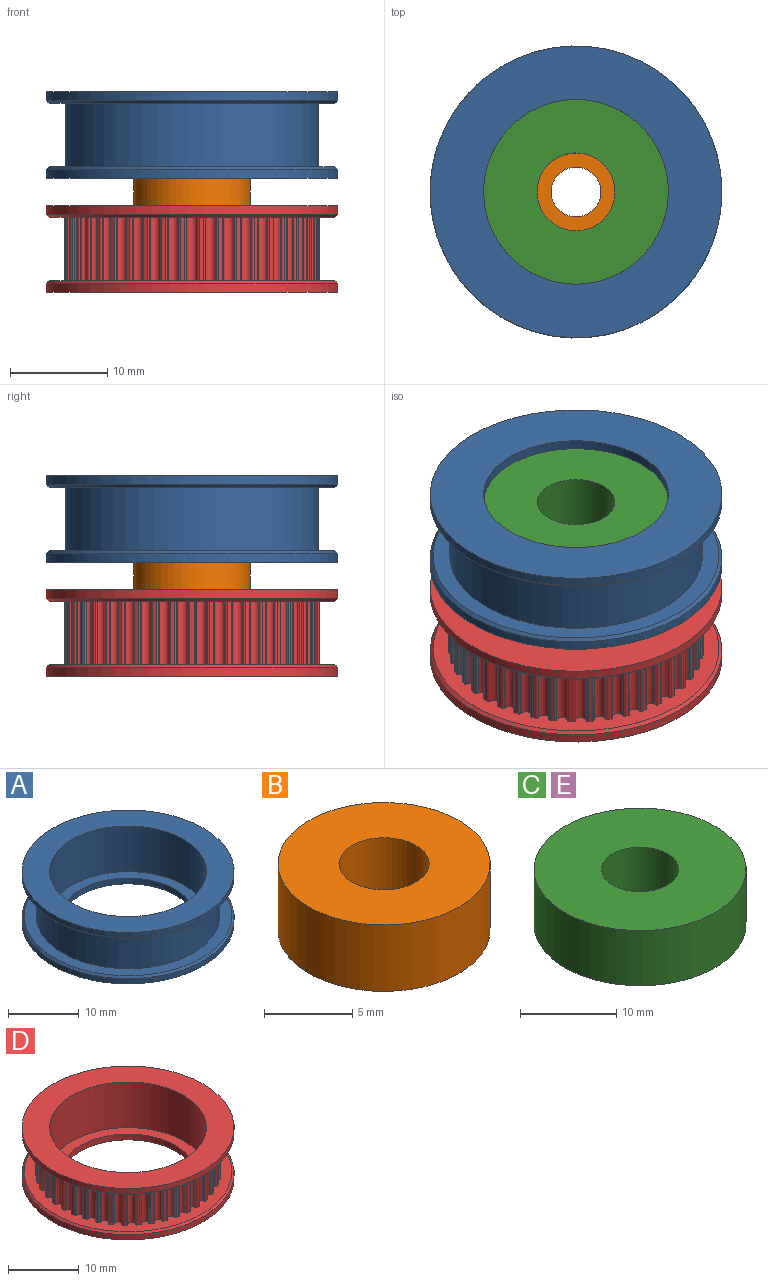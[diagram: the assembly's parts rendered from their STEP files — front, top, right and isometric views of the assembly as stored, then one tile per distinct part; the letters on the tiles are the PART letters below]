
ASSEMBLY  parts=5 mates=4
PART A: 12 faces, bbox 30x30x8.9 mm
  f0: plane 30x30mm, normal (0,0,1), area 319.8mm2, adj f6,f8
  f1: plane 30x30mm, normal (0,0,-1), area 423.3mm2, adj f2,f7
  f2: cylinder r=15mm len=30mm, axis (0,0,1), area 84.8mm2, adj f1,f11
  f3: plane 29.4x29.4mm, normal (0,0,1), area 147.9mm2, adj f4,f11
  f4: cylinder r=13mm len=26mm, axis (0,0,1), area 530.9mm2, adj f3,f5
  f5: plane 29.4x29.4mm, normal (0,0,-1), area 147.9mm2, adj f4,f10
  f6: cylinder r=15mm len=30mm, axis (0,0,1), area 84.8mm2, adj f0,f10
  f7: cylinder r=9.5mm len=19mm, axis (0,0,1), area 59.7mm2, adj f1,f9
  f8: cylinder r=11.1mm len=22.2mm, axis (0,0,1), area 551mm2, adj f0,f9
  f9: plane 22.2x22.2mm, normal (0,0,1), area 103.5mm2, adj f7,f8
  f10: cone r=15mm half-angle=45deg, axis (0,0,1), area 39.6mm2, adj f5,f6
  f11: cone r=14.7mm half-angle=45deg, axis (0,0,-1), area 39.6mm2, adj f2,f3
PART B: 4 faces, bbox 12x12x4.6 mm
  f0: cylinder r=2.55mm len=5.1mm, axis (0,0,-1), area 73.7mm2, adj f2,f3
  f1: cylinder r=6mm len=12mm, axis (0,0,-1), area 173.4mm2, adj f2,f3
  f2: plane 12x12mm, normal (0,0,1), area 92.7mm2, adj f0,f1
  f3: plane 12x12mm, normal (0,0,-1), area 92.7mm2, adj f0,f1
PART C: 4 faces, bbox 22x22x7 mm
  f0: cylinder r=4mm len=8mm, axis (0,0,-1), area 175.9mm2, adj f2,f3
  f1: cylinder r=11mm len=22mm, axis (0,0,-1), area 483.8mm2, adj f2,f3
  f2: plane 22x22mm, normal (0,0,1), area 329.9mm2, adj f0,f1
  f3: plane 22x22mm, normal (0,0,-1), area 329.9mm2, adj f0,f1
PART D: 263 faces, bbox 30x30x8.9 mm
  f0: cylinder r=13.12mm len=6.5mm, axis (0,0,-1), area 2.7mm2, adj f1,f12,f252,f255
  f1: cylinder r=0.19mm len=6.5mm, axis (0,0,-1), area 1.7mm2, adj f0,f2,f252,f255
  f2: cylinder r=5mm len=6.5mm, axis (0,0,-1), area 1.2mm2, adj f1,f3,f252,f255
  f3: cylinder r=0.56mm len=6.5mm, axis (0,0,-1), area 9.4mm2, adj f2,f4,f252,f255
  f4: cylinder r=5mm len=6.5mm, axis (0,0,-1), area 1.2mm2, adj f3,f5,f252,f255
  f5: cylinder r=0.19mm len=6.5mm, axis (0,0,-1), area 1.7mm2, adj f4,f6,f252,f255
  f6: cylinder r=13.12mm len=6.5mm, axis (0,0,-1), area 2.7mm2, adj f5,f247,f252,f255
  f7: cylinder r=13.12mm len=6.5mm, axis (0,0,-1), area 2.7mm2, adj f8,f18,f252,f255
  f8: cylinder r=0.19mm len=6.5mm, axis (0,0,-1), area 1.7mm2, adj f7,f9,f252,f255
  f9: cylinder r=5mm len=6.5mm, axis (0,0,-1), area 1.2mm2, adj f8,f10,f252,f255
  f10: cylinder r=0.56mm len=6.5mm, axis (0,0,-1), area 9.4mm2, adj f9,f11,f252,f255
  f11: cylinder r=5mm len=6.5mm, axis (0,0,-1), area 1.2mm2, adj f10,f12,f252,f255
  f12: cylinder r=0.19mm len=6.5mm, axis (0,0,-1), area 1.7mm2, adj f0,f11,f252,f255
  f13: cylinder r=13.12mm len=6.5mm, axis (0,0,-1), area 2.7mm2, adj f14,f24,f252,f255
  f14: cylinder r=0.19mm len=6.5mm, axis (0,0,-1), area 1.7mm2, adj f13,f15,f252,f255
  f15: cylinder r=5mm len=6.5mm, axis (0,0,-1), area 1.2mm2, adj f14,f16,f252,f255
  f16: cylinder r=0.56mm len=6.5mm, axis (0,0,-1), area 9.4mm2, adj f15,f17,f252,f255
  f17: cylinder r=5mm len=6.5mm, axis (0,0,-1), area 1.2mm2, adj f16,f18,f252,f255
  f18: cylinder r=0.19mm len=6.5mm, axis (0,0,-1), area 1.7mm2, adj f7,f17,f252,f255
  f19: cylinder r=13.12mm len=6.5mm, axis (0,0,-1), area 2.7mm2, adj f20,f30,f252,f255
  f20: cylinder r=0.19mm len=6.5mm, axis (0,0,-1), area 1.7mm2, adj f19,f21,f252,f255
  f21: cylinder r=5mm len=6.5mm, axis (0,0,-1), area 1.2mm2, adj f20,f22,f252,f255
  f22: cylinder r=0.56mm len=6.5mm, axis (0,0,-1), area 9.4mm2, adj f21,f23,f252,f255
  f23: cylinder r=5mm len=6.5mm, axis (0,0,-1), area 1.2mm2, adj f22,f24,f252,f255
  f24: cylinder r=0.19mm len=6.5mm, axis (0,0,-1), area 1.7mm2, adj f13,f23,f252,f255
  f25: cylinder r=13.12mm len=6.5mm, axis (0,0,-1), area 2.7mm2, adj f26,f36,f252,f255
  f26: cylinder r=0.19mm len=6.5mm, axis (0,0,-1), area 1.7mm2, adj f25,f27,f252,f255
  f27: cylinder r=5mm len=6.5mm, axis (0,0,-1), area 1.2mm2, adj f26,f28,f252,f255
  f28: cylinder r=0.56mm len=6.5mm, axis (0,0,-1), area 9.4mm2, adj f27,f29,f252,f255
  f29: cylinder r=5mm len=6.5mm, axis (0,0,-1), area 1.2mm2, adj f28,f30,f252,f255
  f30: cylinder r=0.19mm len=6.5mm, axis (0,0,-1), area 1.7mm2, adj f19,f29,f252,f255
  f31: cylinder r=13.12mm len=6.5mm, axis (0,0,-1), area 2.7mm2, adj f32,f42,f252,f255
  f32: cylinder r=0.19mm len=6.5mm, axis (0,0,-1), area 1.7mm2, adj f31,f33,f252,f255
  f33: cylinder r=5mm len=6.5mm, axis (0,0,-1), area 1.2mm2, adj f32,f34,f252,f255
  f34: cylinder r=0.56mm len=6.5mm, axis (0,0,-1), area 9.4mm2, adj f33,f35,f252,f255
  f35: cylinder r=5mm len=6.5mm, axis (0,0,-1), area 1.2mm2, adj f34,f36,f252,f255
  f36: cylinder r=0.19mm len=6.5mm, axis (0,0,-1), area 1.7mm2, adj f25,f35,f252,f255
  f37: cylinder r=13.12mm len=6.5mm, axis (0,0,-1), area 2.7mm2, adj f38,f48,f252,f255
  f38: cylinder r=0.19mm len=6.5mm, axis (0,0,-1), area 1.7mm2, adj f37,f39,f252,f255
  f39: cylinder r=5mm len=6.5mm, axis (0,0,-1), area 1.2mm2, adj f38,f40,f252,f255
  f40: cylinder r=0.56mm len=6.5mm, axis (0,0,-1), area 9.4mm2, adj f39,f41,f252,f255
  f41: cylinder r=5mm len=6.5mm, axis (0,0,-1), area 1.2mm2, adj f40,f42,f252,f255
  f42: cylinder r=0.19mm len=6.5mm, axis (0,0,-1), area 1.7mm2, adj f31,f41,f252,f255
  f43: cylinder r=13.12mm len=6.5mm, axis (0,0,-1), area 2.7mm2, adj f44,f54,f252,f255
  f44: cylinder r=0.19mm len=6.5mm, axis (0,0,-1), area 1.7mm2, adj f43,f45,f252,f255
  f45: cylinder r=5mm len=6.5mm, axis (0,0,-1), area 1.2mm2, adj f44,f46,f252,f255
  f46: cylinder r=0.56mm len=6.5mm, axis (0,0,-1), area 9.4mm2, adj f45,f47,f252,f255
  f47: cylinder r=5mm len=6.5mm, axis (0,0,-1), area 1.2mm2, adj f46,f48,f252,f255
  f48: cylinder r=0.19mm len=6.5mm, axis (0,0,-1), area 1.7mm2, adj f37,f47,f252,f255
  f49: cylinder r=13.12mm len=6.5mm, axis (0,0,-1), area 2.7mm2, adj f50,f60,f252,f255
  f50: cylinder r=0.19mm len=6.5mm, axis (0,0,-1), area 1.7mm2, adj f49,f51,f252,f255
  f51: cylinder r=5mm len=6.5mm, axis (0,0,-1), area 1.2mm2, adj f50,f52,f252,f255
  f52: cylinder r=0.56mm len=6.5mm, axis (0,0,-1), area 9.4mm2, adj f51,f53,f252,f255
  f53: cylinder r=5mm len=6.5mm, axis (0,0,-1), area 1.2mm2, adj f52,f54,f252,f255
  f54: cylinder r=0.19mm len=6.5mm, axis (0,0,-1), area 1.7mm2, adj f43,f53,f252,f255
  f55: cylinder r=13.12mm len=6.5mm, axis (0,0,-1), area 2.7mm2, adj f56,f66,f252,f255
  f56: cylinder r=0.19mm len=6.5mm, axis (0,0,-1), area 1.7mm2, adj f55,f57,f252,f255
  f57: cylinder r=5mm len=6.5mm, axis (0,0,-1), area 1.2mm2, adj f56,f58,f252,f255
  f58: cylinder r=0.56mm len=6.5mm, axis (0,0,-1), area 9.4mm2, adj f57,f59,f252,f255
  f59: cylinder r=5mm len=6.5mm, axis (0,0,-1), area 1.2mm2, adj f58,f60,f252,f255
  f60: cylinder r=0.19mm len=6.5mm, axis (0,0,-1), area 1.7mm2, adj f49,f59,f252,f255
  f61: cylinder r=13.12mm len=6.5mm, axis (0,0,-1), area 2.7mm2, adj f62,f72,f252,f255
  f62: cylinder r=0.19mm len=6.5mm, axis (0,0,-1), area 1.7mm2, adj f61,f63,f252,f255
  f63: cylinder r=5mm len=6.5mm, axis (0,0,-1), area 1.2mm2, adj f62,f64,f252,f255
  f64: cylinder r=0.56mm len=6.5mm, axis (0,0,-1), area 9.4mm2, adj f63,f65,f252,f255
  f65: cylinder r=5mm len=6.5mm, axis (0,0,-1), area 1.2mm2, adj f64,f66,f252,f255
  f66: cylinder r=0.19mm len=6.5mm, axis (0,0,-1), area 1.7mm2, adj f55,f65,f252,f255
  f67: cylinder r=13.12mm len=6.5mm, axis (0,0,-1), area 2.7mm2, adj f68,f78,f252,f255
  f68: cylinder r=0.19mm len=6.5mm, axis (0,0,-1), area 1.7mm2, adj f67,f69,f252,f255
  f69: cylinder r=5mm len=6.5mm, axis (0,0,-1), area 1.2mm2, adj f68,f70,f252,f255
  f70: cylinder r=0.56mm len=6.5mm, axis (0,0,-1), area 9.4mm2, adj f69,f71,f252,f255
  f71: cylinder r=5mm len=6.5mm, axis (0,0,-1), area 1.2mm2, adj f70,f72,f252,f255
  f72: cylinder r=0.19mm len=6.5mm, axis (0,0,-1), area 1.7mm2, adj f61,f71,f252,f255
  f73: cylinder r=13.12mm len=6.5mm, axis (0,0,-1), area 2.7mm2, adj f74,f84,f252,f255
  f74: cylinder r=0.19mm len=6.5mm, axis (0,0,-1), area 1.7mm2, adj f73,f75,f252,f255
  f75: cylinder r=5mm len=6.5mm, axis (0,0,-1), area 1.2mm2, adj f74,f76,f252,f255
  f76: cylinder r=0.56mm len=6.5mm, axis (0,0,-1), area 9.4mm2, adj f75,f77,f252,f255
  f77: cylinder r=5mm len=6.5mm, axis (0,0,-1), area 1.2mm2, adj f76,f78,f252,f255
  f78: cylinder r=0.19mm len=6.5mm, axis (0,0,-1), area 1.7mm2, adj f67,f77,f252,f255
  f79: cylinder r=13.12mm len=6.5mm, axis (0,0,-1), area 2.7mm2, adj f80,f90,f252,f255
  f80: cylinder r=0.19mm len=6.5mm, axis (0,0,-1), area 1.7mm2, adj f79,f81,f252,f255
  f81: cylinder r=5mm len=6.5mm, axis (0,0,-1), area 1.2mm2, adj f80,f82,f252,f255
  f82: cylinder r=0.56mm len=6.5mm, axis (0,0,-1), area 9.4mm2, adj f81,f83,f252,f255
  f83: cylinder r=5mm len=6.5mm, axis (0,0,-1), area 1.2mm2, adj f82,f84,f252,f255
  f84: cylinder r=0.19mm len=6.5mm, axis (0,0,-1), area 1.7mm2, adj f73,f83,f252,f255
  f85: cylinder r=13.12mm len=6.5mm, axis (0,0,-1), area 2.7mm2, adj f86,f96,f252,f255
  f86: cylinder r=0.19mm len=6.5mm, axis (0,0,-1), area 1.7mm2, adj f85,f87,f252,f255
  f87: cylinder r=5mm len=6.5mm, axis (0,0,-1), area 1.2mm2, adj f86,f88,f252,f255
  f88: cylinder r=0.56mm len=6.5mm, axis (0,0,-1), area 9.4mm2, adj f87,f89,f252,f255
  f89: cylinder r=5mm len=6.5mm, axis (0,0,-1), area 1.2mm2, adj f88,f90,f252,f255
  f90: cylinder r=0.19mm len=6.5mm, axis (0,0,-1), area 1.7mm2, adj f79,f89,f252,f255
  f91: cylinder r=13.12mm len=6.5mm, axis (0,0,-1), area 2.7mm2, adj f92,f102,f252,f255
  f92: cylinder r=0.19mm len=6.5mm, axis (0,0,-1), area 1.7mm2, adj f91,f93,f252,f255
  f93: cylinder r=5mm len=6.5mm, axis (0,0,-1), area 1.2mm2, adj f92,f94,f252,f255
  f94: cylinder r=0.56mm len=6.5mm, axis (0,0,-1), area 9.4mm2, adj f93,f95,f252,f255
  f95: cylinder r=5mm len=6.5mm, axis (0,0,-1), area 1.2mm2, adj f94,f96,f252,f255
  f96: cylinder r=0.19mm len=6.5mm, axis (0,0,-1), area 1.7mm2, adj f85,f95,f252,f255
  f97: cylinder r=13.12mm len=6.5mm, axis (0,0,-1), area 2.7mm2, adj f98,f108,f252,f255
  f98: cylinder r=0.19mm len=6.5mm, axis (0,0,-1), area 1.7mm2, adj f97,f99,f252,f255
  f99: cylinder r=5mm len=6.5mm, axis (0,0,-1), area 1.2mm2, adj f98,f100,f252,f255
  f100: cylinder r=0.56mm len=6.5mm, axis (0,0,-1), area 9.4mm2, adj f99,f101,f252,f255
  f101: cylinder r=5mm len=6.5mm, axis (0,0,-1), area 1.2mm2, adj f100,f102,f252,f255
  f102: cylinder r=0.19mm len=6.5mm, axis (0,0,-1), area 1.7mm2, adj f91,f101,f252,f255
  f103: cylinder r=13.12mm len=6.5mm, axis (0,0,-1), area 2.7mm2, adj f104,f114,f252,f255
  f104: cylinder r=0.19mm len=6.5mm, axis (0,0,-1), area 1.7mm2, adj f103,f105,f252,f255
  f105: cylinder r=5mm len=6.5mm, axis (0,0,-1), area 1.2mm2, adj f104,f106,f252,f255
  f106: cylinder r=0.56mm len=6.5mm, axis (0,0,-1), area 9.4mm2, adj f105,f107,f252,f255
  f107: cylinder r=5mm len=6.5mm, axis (0,0,-1), area 1.2mm2, adj f106,f108,f252,f255
  f108: cylinder r=0.19mm len=6.5mm, axis (0,0,-1), area 1.7mm2, adj f97,f107,f252,f255
  f109: cylinder r=13.12mm len=6.5mm, axis (0,0,-1), area 2.7mm2, adj f110,f120,f252,f255
  f110: cylinder r=0.19mm len=6.5mm, axis (0,0,-1), area 1.7mm2, adj f109,f111,f252,f255
  f111: cylinder r=5mm len=6.5mm, axis (0,0,-1), area 1.2mm2, adj f110,f112,f252,f255
  f112: cylinder r=0.56mm len=6.5mm, axis (0,0,-1), area 9.4mm2, adj f111,f113,f252,f255
  f113: cylinder r=5mm len=6.5mm, axis (0,0,-1), area 1.2mm2, adj f112,f114,f252,f255
  f114: cylinder r=0.19mm len=6.5mm, axis (0,0,-1), area 1.7mm2, adj f103,f113,f252,f255
  f115: cylinder r=13.12mm len=6.5mm, axis (0,0,-1), area 2.7mm2, adj f116,f126,f252,f255
  f116: cylinder r=0.19mm len=6.5mm, axis (0,0,-1), area 1.7mm2, adj f115,f117,f252,f255
  f117: cylinder r=5mm len=6.5mm, axis (0,0,-1), area 1.2mm2, adj f116,f118,f252,f255
  f118: cylinder r=0.56mm len=6.5mm, axis (0,0,-1), area 9.4mm2, adj f117,f119,f252,f255
  f119: cylinder r=5mm len=6.5mm, axis (0,0,-1), area 1.2mm2, adj f118,f120,f252,f255
  f120: cylinder r=0.19mm len=6.5mm, axis (0,0,-1), area 1.7mm2, adj f109,f119,f252,f255
  f121: cylinder r=13.12mm len=6.5mm, axis (0,0,-1), area 2.7mm2, adj f122,f132,f252,f255
  f122: cylinder r=0.19mm len=6.5mm, axis (0,0,-1), area 1.7mm2, adj f121,f123,f252,f255
  f123: cylinder r=5mm len=6.5mm, axis (0,0,-1), area 1.2mm2, adj f122,f124,f252,f255
  f124: cylinder r=0.56mm len=6.5mm, axis (0,0,-1), area 9.4mm2, adj f123,f125,f252,f255
  f125: cylinder r=5mm len=6.5mm, axis (0,0,-1), area 1.2mm2, adj f124,f126,f252,f255
  f126: cylinder r=0.19mm len=6.5mm, axis (0,0,-1), area 1.7mm2, adj f115,f125,f252,f255
  f127: cylinder r=13.12mm len=6.5mm, axis (0,0,-1), area 2.7mm2, adj f128,f138,f252,f255
  f128: cylinder r=0.19mm len=6.5mm, axis (0,0,-1), area 1.7mm2, adj f127,f129,f252,f255
  f129: cylinder r=5mm len=6.5mm, axis (0,0,-1), area 1.2mm2, adj f128,f130,f252,f255
  f130: cylinder r=0.56mm len=6.5mm, axis (0,0,-1), area 9.4mm2, adj f129,f131,f252,f255
  f131: cylinder r=5mm len=6.5mm, axis (0,0,-1), area 1.2mm2, adj f130,f132,f252,f255
  f132: cylinder r=0.19mm len=6.5mm, axis (0,0,-1), area 1.7mm2, adj f121,f131,f252,f255
  f133: cylinder r=13.12mm len=6.5mm, axis (0,0,-1), area 2.7mm2, adj f134,f144,f252,f255
  f134: cylinder r=0.19mm len=6.5mm, axis (0,0,-1), area 1.7mm2, adj f133,f135,f252,f255
  f135: cylinder r=5mm len=6.5mm, axis (0,0,-1), area 1.2mm2, adj f134,f136,f252,f255
  f136: cylinder r=0.56mm len=6.5mm, axis (0,0,-1), area 9.4mm2, adj f135,f137,f252,f255
  f137: cylinder r=5mm len=6.5mm, axis (0,0,-1), area 1.2mm2, adj f136,f138,f252,f255
  f138: cylinder r=0.19mm len=6.5mm, axis (0,0,-1), area 1.7mm2, adj f127,f137,f252,f255
  f139: cylinder r=13.12mm len=6.5mm, axis (0,0,-1), area 2.7mm2, adj f140,f150,f252,f255
  f140: cylinder r=0.19mm len=6.5mm, axis (0,0,-1), area 1.7mm2, adj f139,f141,f252,f255
  f141: cylinder r=5mm len=6.5mm, axis (0,0,-1), area 1.2mm2, adj f140,f142,f252,f255
  f142: cylinder r=0.56mm len=6.5mm, axis (0,0,-1), area 9.4mm2, adj f141,f143,f252,f255
  f143: cylinder r=5mm len=6.5mm, axis (0,0,-1), area 1.2mm2, adj f142,f144,f252,f255
  f144: cylinder r=0.19mm len=6.5mm, axis (0,0,-1), area 1.7mm2, adj f133,f143,f252,f255
  f145: cylinder r=13.12mm len=6.5mm, axis (0,0,-1), area 2.7mm2, adj f146,f156,f252,f255
  f146: cylinder r=0.19mm len=6.5mm, axis (0,0,-1), area 1.7mm2, adj f145,f147,f252,f255
  f147: cylinder r=5mm len=6.5mm, axis (0,0,-1), area 1.2mm2, adj f146,f148,f252,f255
  f148: cylinder r=0.56mm len=6.5mm, axis (0,0,-1), area 9.4mm2, adj f147,f149,f252,f255
  f149: cylinder r=5mm len=6.5mm, axis (0,0,-1), area 1.2mm2, adj f148,f150,f252,f255
  f150: cylinder r=0.19mm len=6.5mm, axis (0,0,-1), area 1.7mm2, adj f139,f149,f252,f255
  f151: cylinder r=13.12mm len=6.5mm, axis (0,0,-1), area 2.7mm2, adj f152,f162,f252,f255
  f152: cylinder r=0.19mm len=6.5mm, axis (0,0,-1), area 1.7mm2, adj f151,f153,f252,f255
  f153: cylinder r=5mm len=6.5mm, axis (0,0,-1), area 1.2mm2, adj f152,f154,f252,f255
  f154: cylinder r=0.56mm len=6.5mm, axis (0,0,-1), area 9.4mm2, adj f153,f155,f252,f255
  f155: cylinder r=5mm len=6.5mm, axis (0,0,-1), area 1.2mm2, adj f154,f156,f252,f255
  f156: cylinder r=0.19mm len=6.5mm, axis (0,0,-1), area 1.7mm2, adj f145,f155,f252,f255
  f157: cylinder r=13.12mm len=6.5mm, axis (0,0,-1), area 2.7mm2, adj f158,f168,f252,f255
  f158: cylinder r=0.19mm len=6.5mm, axis (0,0,-1), area 1.7mm2, adj f157,f159,f252,f255
  f159: cylinder r=5mm len=6.5mm, axis (0,0,-1), area 1.2mm2, adj f158,f160,f252,f255
  f160: cylinder r=0.56mm len=6.5mm, axis (0,0,-1), area 9.4mm2, adj f159,f161,f252,f255
  f161: cylinder r=5mm len=6.5mm, axis (0,0,-1), area 1.2mm2, adj f160,f162,f252,f255
  f162: cylinder r=0.19mm len=6.5mm, axis (0,0,-1), area 1.7mm2, adj f151,f161,f252,f255
  f163: cylinder r=13.12mm len=6.5mm, axis (0,0,-1), area 2.7mm2, adj f164,f174,f252,f255
  f164: cylinder r=0.19mm len=6.5mm, axis (0,0,-1), area 1.7mm2, adj f163,f165,f252,f255
  f165: cylinder r=5mm len=6.5mm, axis (0,0,-1), area 1.2mm2, adj f164,f166,f252,f255
  f166: cylinder r=0.56mm len=6.5mm, axis (0,0,-1), area 9.4mm2, adj f165,f167,f252,f255
  f167: cylinder r=5mm len=6.5mm, axis (0,0,-1), area 1.2mm2, adj f166,f168,f252,f255
  f168: cylinder r=0.19mm len=6.5mm, axis (0,0,-1), area 1.7mm2, adj f157,f167,f252,f255
  f169: cylinder r=13.12mm len=6.5mm, axis (0,0,-1), area 2.7mm2, adj f170,f180,f252,f255
  f170: cylinder r=0.19mm len=6.5mm, axis (0,0,-1), area 1.7mm2, adj f169,f171,f252,f255
  f171: cylinder r=5mm len=6.5mm, axis (0,0,-1), area 1.2mm2, adj f170,f172,f252,f255
  f172: cylinder r=0.56mm len=6.5mm, axis (0,0,-1), area 9.4mm2, adj f171,f173,f252,f255
  f173: cylinder r=5mm len=6.5mm, axis (0,0,-1), area 1.2mm2, adj f172,f174,f252,f255
  f174: cylinder r=0.19mm len=6.5mm, axis (0,0,-1), area 1.7mm2, adj f163,f173,f252,f255
  f175: cylinder r=13.12mm len=6.5mm, axis (0,0,-1), area 2.7mm2, adj f176,f186,f252,f255
  f176: cylinder r=0.19mm len=6.5mm, axis (0,0,-1), area 1.7mm2, adj f175,f177,f252,f255
  f177: cylinder r=5mm len=6.5mm, axis (0,0,-1), area 1.2mm2, adj f176,f178,f252,f255
  f178: cylinder r=0.56mm len=6.5mm, axis (0,0,-1), area 9.4mm2, adj f177,f179,f252,f255
  f179: cylinder r=5mm len=6.5mm, axis (0,0,-1), area 1.2mm2, adj f178,f180,f252,f255
  f180: cylinder r=0.19mm len=6.5mm, axis (0,0,-1), area 1.7mm2, adj f169,f179,f252,f255
  f181: cylinder r=13.12mm len=6.5mm, axis (0,0,-1), area 2.7mm2, adj f182,f192,f252,f255
  f182: cylinder r=0.19mm len=6.5mm, axis (0,0,-1), area 1.7mm2, adj f181,f183,f252,f255
  f183: cylinder r=5mm len=6.5mm, axis (0,0,-1), area 1.2mm2, adj f182,f184,f252,f255
  f184: cylinder r=0.56mm len=6.5mm, axis (0,0,-1), area 9.4mm2, adj f183,f185,f252,f255
  f185: cylinder r=5mm len=6.5mm, axis (0,0,-1), area 1.2mm2, adj f184,f186,f252,f255
  f186: cylinder r=0.19mm len=6.5mm, axis (0,0,-1), area 1.7mm2, adj f175,f185,f252,f255
  f187: cylinder r=13.12mm len=6.5mm, axis (0,0,-1), area 2.7mm2, adj f188,f198,f252,f255
  f188: cylinder r=0.19mm len=6.5mm, axis (0,0,-1), area 1.7mm2, adj f187,f189,f252,f255
  f189: cylinder r=5mm len=6.5mm, axis (0,0,-1), area 1.2mm2, adj f188,f190,f252,f255
  f190: cylinder r=0.56mm len=6.5mm, axis (0,0,-1), area 9.4mm2, adj f189,f191,f252,f255
  f191: cylinder r=5mm len=6.5mm, axis (0,0,-1), area 1.2mm2, adj f190,f192,f252,f255
  f192: cylinder r=0.19mm len=6.5mm, axis (0,0,-1), area 1.7mm2, adj f181,f191,f252,f255
  f193: cylinder r=13.12mm len=6.5mm, axis (0,0,-1), area 2.7mm2, adj f194,f204,f252,f255
  f194: cylinder r=0.19mm len=6.5mm, axis (0,0,-1), area 1.7mm2, adj f193,f195,f252,f255
  f195: cylinder r=5mm len=6.5mm, axis (0,0,-1), area 1.2mm2, adj f194,f196,f252,f255
  f196: cylinder r=0.56mm len=6.5mm, axis (0,0,-1), area 9.4mm2, adj f195,f197,f252,f255
  f197: cylinder r=5mm len=6.5mm, axis (0,0,-1), area 1.2mm2, adj f196,f198,f252,f255
  f198: cylinder r=0.19mm len=6.5mm, axis (0,0,-1), area 1.7mm2, adj f187,f197,f252,f255
  f199: cylinder r=13.12mm len=6.5mm, axis (0,0,-1), area 2.7mm2, adj f200,f210,f252,f255
  f200: cylinder r=0.19mm len=6.5mm, axis (0,0,-1), area 1.7mm2, adj f199,f201,f252,f255
  f201: cylinder r=5mm len=6.5mm, axis (0,0,-1), area 1.2mm2, adj f200,f202,f252,f255
  f202: cylinder r=0.56mm len=6.5mm, axis (0,0,-1), area 9.4mm2, adj f201,f203,f252,f255
  f203: cylinder r=5mm len=6.5mm, axis (0,0,-1), area 1.2mm2, adj f202,f204,f252,f255
  f204: cylinder r=0.19mm len=6.5mm, axis (0,0,-1), area 1.7mm2, adj f193,f203,f252,f255
  f205: cylinder r=13.12mm len=6.5mm, axis (0,0,-1), area 2.7mm2, adj f206,f216,f252,f255
  f206: cylinder r=0.19mm len=6.5mm, axis (0,0,-1), area 1.7mm2, adj f205,f207,f252,f255
  f207: cylinder r=5mm len=6.5mm, axis (0,0,-1), area 1.2mm2, adj f206,f208,f252,f255
  f208: cylinder r=0.56mm len=6.5mm, axis (0,0,-1), area 9.4mm2, adj f207,f209,f252,f255
  f209: cylinder r=5mm len=6.5mm, axis (0,0,-1), area 1.2mm2, adj f208,f210,f252,f255
  f210: cylinder r=0.19mm len=6.5mm, axis (0,0,-1), area 1.7mm2, adj f199,f209,f252,f255
  f211: cylinder r=13.12mm len=6.5mm, axis (0,0,-1), area 2.7mm2, adj f212,f222,f252,f255
  f212: cylinder r=0.19mm len=6.5mm, axis (0,0,-1), area 1.7mm2, adj f211,f213,f252,f255
  f213: cylinder r=5mm len=6.5mm, axis (0,0,-1), area 1.2mm2, adj f212,f214,f252,f255
  f214: cylinder r=0.56mm len=6.5mm, axis (0,0,-1), area 9.4mm2, adj f213,f215,f252,f255
  f215: cylinder r=5mm len=6.5mm, axis (0,0,-1), area 1.2mm2, adj f214,f216,f252,f255
  f216: cylinder r=0.19mm len=6.5mm, axis (0,0,-1), area 1.7mm2, adj f205,f215,f252,f255
  f217: cylinder r=13.12mm len=6.5mm, axis (0,0,-1), area 2.7mm2, adj f218,f228,f252,f255
  f218: cylinder r=0.19mm len=6.5mm, axis (0,0,-1), area 1.7mm2, adj f217,f219,f252,f255
  f219: cylinder r=5mm len=6.5mm, axis (0,0,-1), area 1.2mm2, adj f218,f220,f252,f255
  f220: cylinder r=0.56mm len=6.5mm, axis (0,0,-1), area 9.4mm2, adj f219,f221,f252,f255
  f221: cylinder r=5mm len=6.5mm, axis (0,0,-1), area 1.2mm2, adj f220,f222,f252,f255
  f222: cylinder r=0.19mm len=6.5mm, axis (0,0,-1), area 1.7mm2, adj f211,f221,f252,f255
  f223: cylinder r=13.12mm len=6.5mm, axis (0,0,-1), area 2.7mm2, adj f224,f234,f252,f255
  f224: cylinder r=0.19mm len=6.5mm, axis (0,0,-1), area 1.7mm2, adj f223,f225,f252,f255
  f225: cylinder r=5mm len=6.5mm, axis (0,0,-1), area 1.2mm2, adj f224,f226,f252,f255
  f226: cylinder r=0.56mm len=6.5mm, axis (0,0,-1), area 9.4mm2, adj f225,f227,f252,f255
  f227: cylinder r=5mm len=6.5mm, axis (0,0,-1), area 1.2mm2, adj f226,f228,f252,f255
  f228: cylinder r=0.19mm len=6.5mm, axis (0,0,-1), area 1.7mm2, adj f217,f227,f252,f255
  f229: cylinder r=13.12mm len=6.5mm, axis (0,0,-1), area 2.7mm2, adj f230,f240,f252,f255
  f230: cylinder r=0.19mm len=6.5mm, axis (0,0,-1), area 1.7mm2, adj f229,f231,f252,f255
  f231: cylinder r=5mm len=6.5mm, axis (0,0,-1), area 1.2mm2, adj f230,f232,f252,f255
  f232: cylinder r=0.56mm len=6.5mm, axis (0,0,-1), area 9.4mm2, adj f231,f233,f252,f255
  f233: cylinder r=5mm len=6.5mm, axis (0,0,-1), area 1.2mm2, adj f232,f234,f252,f255
  f234: cylinder r=0.19mm len=6.5mm, axis (0,0,-1), area 1.7mm2, adj f223,f233,f252,f255
  f235: cylinder r=13.12mm len=6.5mm, axis (0,0,-1), area 2.7mm2, adj f236,f246,f252,f255
  f236: cylinder r=0.19mm len=6.5mm, axis (0,0,-1), area 1.7mm2, adj f235,f237,f252,f255
  f237: cylinder r=5mm len=6.5mm, axis (0,0,-1), area 1.2mm2, adj f236,f238,f252,f255
  f238: cylinder r=0.56mm len=6.5mm, axis (0,0,-1), area 9.4mm2, adj f237,f239,f252,f255
  f239: cylinder r=5mm len=6.5mm, axis (0,0,-1), area 1.2mm2, adj f238,f240,f252,f255
  f240: cylinder r=0.19mm len=6.5mm, axis (0,0,-1), area 1.7mm2, adj f229,f239,f252,f255
  f241: cylinder r=13.12mm len=6.5mm, axis (0,0,-1), area 2.7mm2, adj f242,f251,f252,f255
  f242: cylinder r=0.19mm len=6.5mm, axis (0,0,-1), area 1.7mm2, adj f241,f243,f252,f255
  f243: cylinder r=5mm len=6.5mm, axis (0,0,-1), area 1.2mm2, adj f242,f244,f252,f255
  f244: cylinder r=0.56mm len=6.5mm, axis (0,0,-1), area 9.4mm2, adj f243,f245,f252,f255
  f245: cylinder r=5mm len=6.5mm, axis (0,0,-1), area 1.2mm2, adj f244,f246,f252,f255
  f246: cylinder r=0.19mm len=6.5mm, axis (0,0,-1), area 1.7mm2, adj f235,f245,f252,f255
  f247: cylinder r=0.19mm len=6.5mm, axis (0,0,-1), area 1.7mm2, adj f6,f248,f252,f255
  f248: cylinder r=5mm len=6.5mm, axis (0,0,-1), area 1.2mm2, adj f247,f249,f252,f255
  f249: cylinder r=0.56mm len=6.5mm, axis (0,0,-1), area 9.4mm2, adj f248,f250,f252,f255
  f250: cylinder r=5mm len=6.5mm, axis (0,0,-1), area 1.2mm2, adj f249,f251,f252,f255
  f251: cylinder r=0.19mm len=6.5mm, axis (0,0,-1), area 1.7mm2, adj f241,f250,f252,f255
  f252: plane 29.4x29.4mm, normal (0,0,1), area 168.8mm2, adj f0,f1,f2,f3,f4,f5,f6,f7
  f253: plane 30x30mm, normal (0,0,-1), area 423.3mm2, adj f254,f260
  f254: cylinder r=15mm len=30mm, axis (0,0,1), area 84.8mm2, adj f253,f262
  f255: plane 29.4x29.4mm, normal (0,0,-1), area 168.8mm2, adj f0,f1,f2,f3,f4,f5,f6,f7
  f256: plane 30x30mm, normal (0,0,1), area 319.8mm2, adj f257,f258
  f257: cylinder r=15mm len=30mm, axis (0,0,1), area 84.8mm2, adj f256,f261
  f258: cylinder r=11.1mm len=22.2mm, axis (0,0,1), area 551mm2, adj f256,f259
  f259: plane 22.2x22.2mm, normal (0,0,1), area 103.5mm2, adj f258,f260
  f260: cylinder r=9.5mm len=19mm, axis (0,0,1), area 59.7mm2, adj f253,f259
  f261: cone r=15mm half-angle=45deg, axis (0,0,1), area 39.6mm2, adj f255,f257
  f262: cone r=14.7mm half-angle=45deg, axis (0,0,-1), area 39.6mm2, adj f252,f254
PART E: same geometry as C
PLACE A rot(axis=(1,0,0),180deg) t=(9.21,2.65,31.31)mm
PLACE B t=(9.21,2.65,23.16)mm
PLACE C t=(9.21,2.65,27.76)mm
PLACE D t=(9.21,2.65,19.61)mm
PLACE E t=(9.21,2.65,16.16)mm
MATE fastened D.f0 <-> E.f0  axis (0,0,1) through (9.21,2.65,16.16)mm
MATE fastened A.f7 <-> C.f0  axis (0,0,-1) through (9.21,2.65,34.76)mm
MATE fastened C.f0 <-> B.f0  axis (0,0,-1) through (9.21,2.65,27.76)mm
MATE fastened B.f0 <-> E.f0  axis (0,0,-1) through (9.21,2.65,23.16)mm
